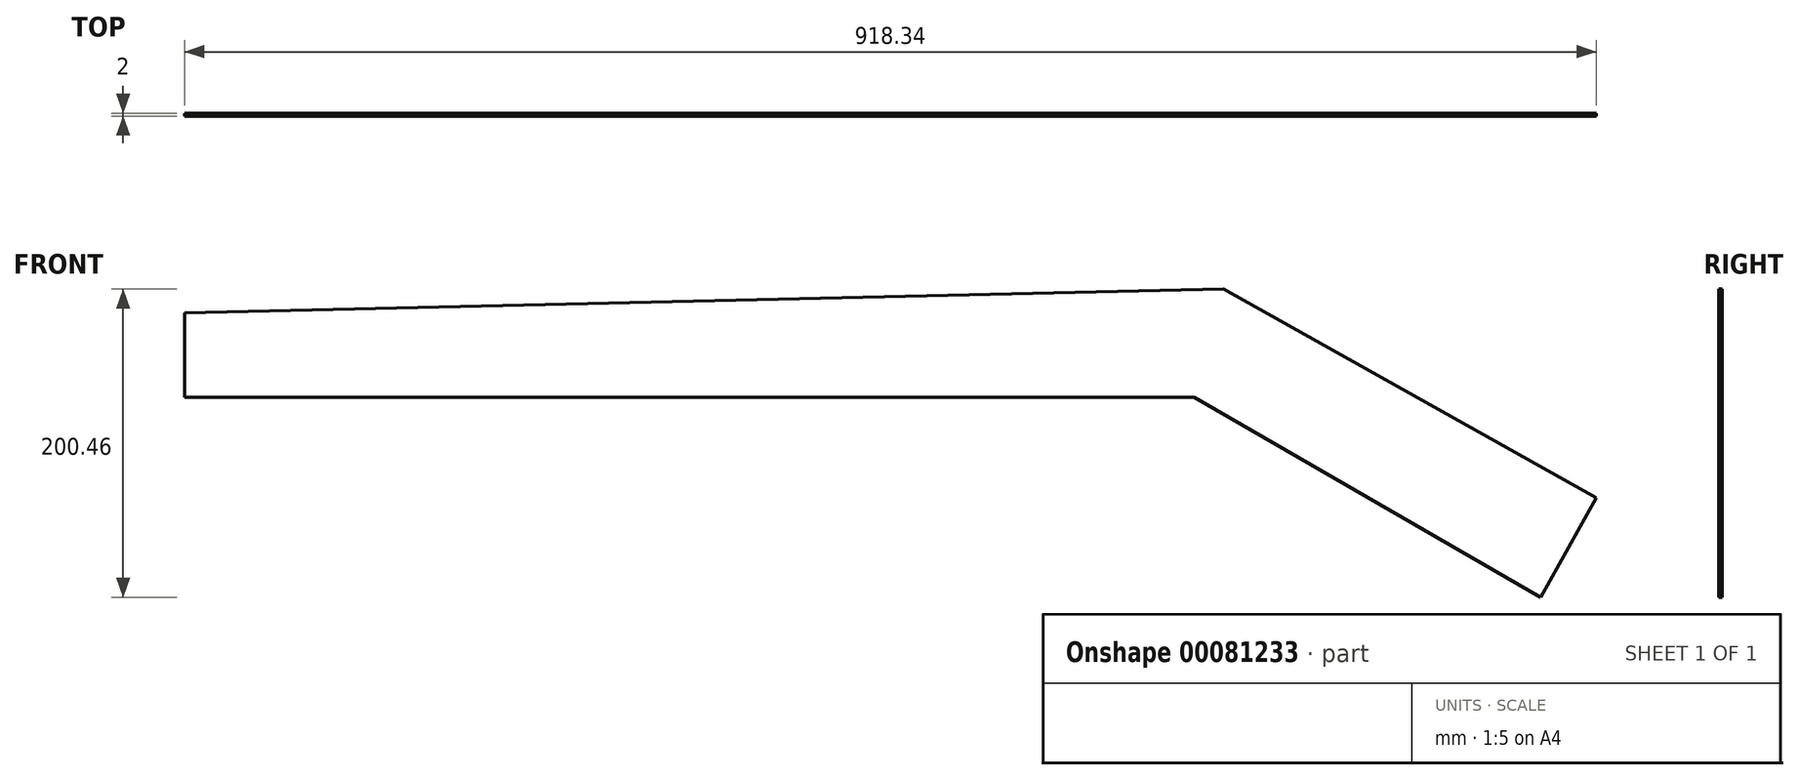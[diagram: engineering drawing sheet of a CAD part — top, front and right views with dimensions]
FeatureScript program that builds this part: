
annotation { "Feature Type Name" : "Feature", "Feature Type Description" : "" }
export const myFeature = defineFeature(function(context is Context, id is Id, definition is map)
    precondition{}
    {
        {
            var Q0;
            Q0=qCreatedBy(makeId("Front.planeOp"),FACE);
            var sketch = newSketch(context, id + "F0", { "sketchPlane" : qUnion([Q0])});
            skLineSegment(sketch, "E0", {"start": v(0, 0) * mm, "end": v(657, 0) * mm});
            skLineSegment(sketch, "E1", {"start": v(0, 0) * mm, "end": v(0, 55) * mm});
            skLineSegment(sketch, "E2", {"start": v(0, 55) * mm, "end": v(675.82, 70.46) * mm});
            skLineSegment(sketch, "E3", {"start": v(657, 0) * mm, "end": v(882.17, -130) * mm});
            skLineSegment(sketch, "E4", {"start": v(675.82, 70.46) * mm, "end": v(918.34, -65.44) * mm});
            skLineSegment(sketch, "E5", {"start": v(882.17, -130) * mm, "end": v(918.34, -65.44) * mm});
            skSolve(sketch);
        }
        {
            var Q0;
            Q0 = qSketchRegion(id + "F0", true);
            extrude(context, id + "F1", {"entities" : qUnion([Q0]), "depth" : 2 * mm});
        }
    });
